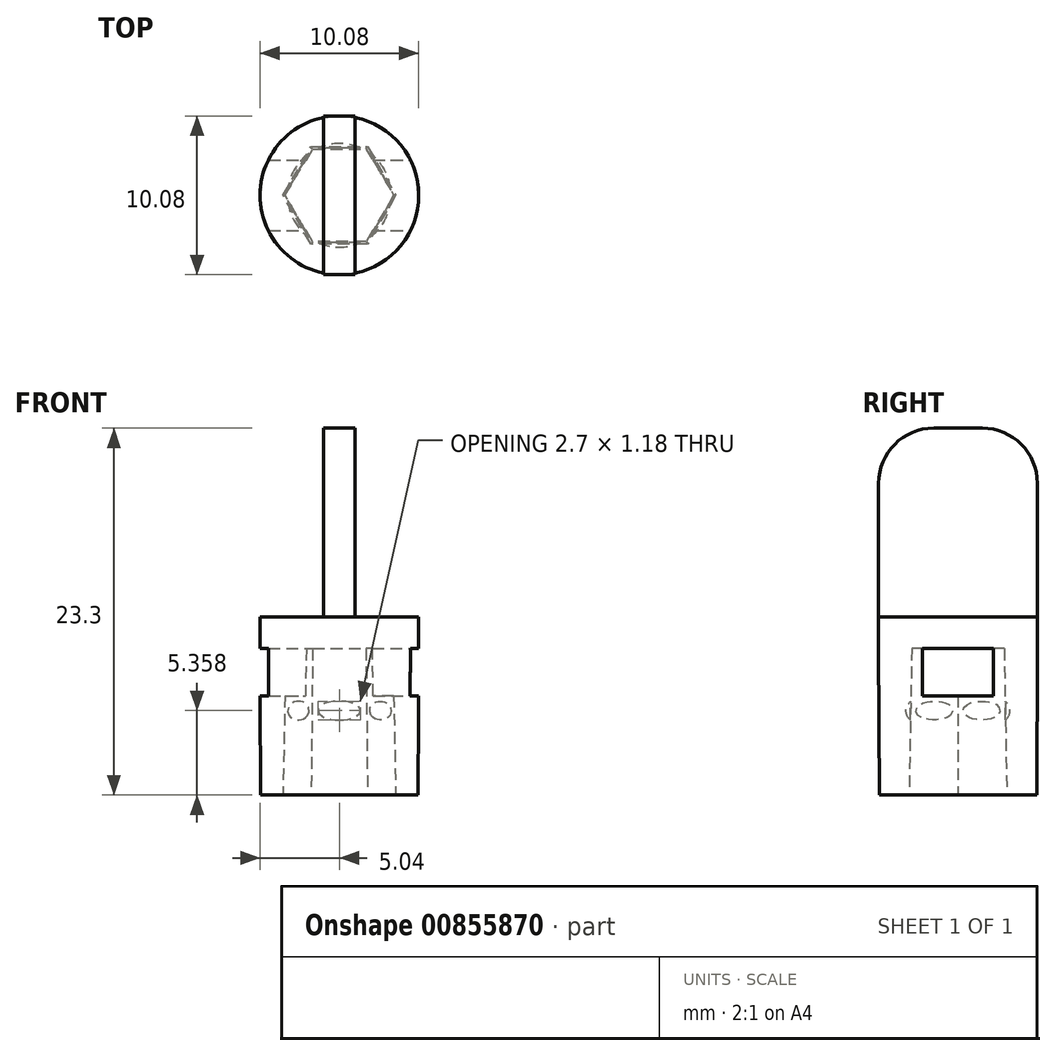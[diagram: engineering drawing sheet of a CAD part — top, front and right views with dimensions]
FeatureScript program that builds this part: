
annotation { "Feature Type Name" : "Feature", "Feature Type Description" : "" }
export const myFeature = defineFeature(function(context is Context, id is Id, definition is map)
    precondition{}
    {
        {
            var Q0;
            Q0=qCreatedBy(makeId("Top.planeOp"),FACE);
            var sketch = newSketch(context, id + "F0", { "sketchPlane" : qUnion([Q0])});
            skCircle(sketch, "E0.cCircle", {"center": v(0, 0) * mm, "radius": 3.1 * mm, "construction": true});
            skLineSegment(sketch, "E0.0", {"start": v(3.58, 0) * mm, "end": v(1.79, -3.1) * mm});
            skLineSegment(sketch, "E0.1", {"start": v(1.79, -3.1) * mm, "end": v(-1.79, -3.1) * mm});
            skLineSegment(sketch, "E0.2", {"start": v(-1.79, -3.1) * mm, "end": v(-3.58, 0) * mm});
            skLineSegment(sketch, "E0.3", {"start": v(-3.58, 0) * mm, "end": v(-1.79, 3.1) * mm});
            skLineSegment(sketch, "E0.4", {"start": v(-1.79, 3.1) * mm, "end": v(1.79, 3.1) * mm});
            skLineSegment(sketch, "E0.5", {"start": v(1.79, 3.1) * mm, "end": v(3.58, 0) * mm});
            skPoint(sketch, "E0.0.midPoint", {"position": v(2.68, -1.55) * mm});
            skCircle(sketch, "E1", {"center": v(0, 0) * mm, "radius": 5 * mm});
            skSolve(sketch);
        }
        {
            var Q0;
            Q0=makeQuery(id+"F0.imprint","IMPRINT",FACE,{"disambiguationData":[TD([[makeQuery(id+"F0.imprint","IMPRINT",EDGE,{"derivedFrom":sQuery(id+"F0.wireOp",EDGE,"E0.0")}),1.0]])]});
            var Q1;
            Q1=makeQuery(id+"F0.imprint","IMPRINT",FACE,{"disambiguationData":[TD([[makeQuery(id+"F0.imprint","IMPRINT",EDGE,{"derivedFrom":sQuery(id+"F0.wireOp",EDGE,"E0.0")}),-1.0]])]});
            extrude(context, id + "F1", {"entities" : qUnion([Q0, Q1]), "depth" : 9.3 * mm, "offsetDistance" : 25 * mm, "hasDraft" : true, "draftAngle" : .25 * degree});
        }
        {
            var Q0;
            Q0=qCreatedBy(makeId("Top.planeOp"),FACE);
            var sketch = newSketch(context, id + "F2", { "sketchPlane" : qUnion([Q0])});
            skCircle(sketch, "E2.cCircle", {"center": v(0, 0) * mm, "radius": 3.1 * mm, "construction": true});
            skLineSegment(sketch, "E2.0", {"start": v(3.58, 0) * mm, "end": v(1.79, -3.1) * mm});
            skLineSegment(sketch, "E2.1", {"start": v(1.79, -3.1) * mm, "end": v(-1.79, -3.1) * mm});
            skLineSegment(sketch, "E2.2", {"start": v(-1.79, -3.1) * mm, "end": v(-3.58, 0) * mm});
            skLineSegment(sketch, "E2.3", {"start": v(-3.58, 0) * mm, "end": v(-1.79, 3.1) * mm});
            skLineSegment(sketch, "E2.4", {"start": v(-1.79, 3.1) * mm, "end": v(1.79, 3.1) * mm});
            skLineSegment(sketch, "E2.5", {"start": v(1.79, 3.1) * mm, "end": v(3.58, 0) * mm});
            skPoint(sketch, "E2.0.midPoint", {"position": v(2.68, -1.55) * mm});
            skCircle(sketch, "E3", {"center": v(0, 0) * mm, "radius": 5 * mm});
            skSolve(sketch);
        }
        {
            var Q0;
            Q0=makeQuery(id+"F2.imprint","IMPRINT",FACE,{"disambiguationData":[TD([[makeQuery(id+"F2.imprint","IMPRINT",EDGE,{"derivedFrom":sQuery(id+"F2.wireOp",EDGE,"E2.0")}),-1.0]])]});
            extrude(context, id + "F3", {"entities" : qUnion([Q0]), "operationType" : NewBodyOperationType.REMOVE, "depth" : 9.3 * mm, "offsetDistance" : 25 * mm, "hasDraft" : true, "draftAngle" : 1 * degree, "draftPullDirection" : true});
        }
        {
            var Q0;
            Q0=qCreatedBy(makeId("Right.planeOp"),FACE);
            var sketch = newSketch(context, id + "F4", { "sketchPlane" : qUnion([Q0])});
            skLineSegment(sketch, "E4", {"start": v(0, 15.23) * mm, "end": v(0, -5.76) * mm, "construction": true});
            skCircle(sketch, "E5", {"center": v(-2.55, 5.35) * mm, "radius": 0.75 * mm});
            skLineSegment(sketch, "E6", {"start": v(12.61, 4.6) * mm, "end": v(-6.83, 4.6) * mm, "construction": true});
            skSolve(sketch);
        }
        {
            var Q0;
            Q0=makeQuery(id+"F4.imprint","IMPRINT",FACE,{"disambiguationData":[TD([[makeQuery(id+"F4.imprint","IMPRINT",EDGE,{"derivedFrom":sQuery(id+"F4.wireOp",EDGE,"E5")}),1.0]])]});
            var Q1;
            Q1=sQuery(id+"F4.wireOp",EDGE,"E4");
            revolve(context, id + "F5", {"operationType" : NewBodyOperationType.REMOVE, "surfaceOperationType" : NewSurfaceOperationType.NEW, "entities" : qUnion([Q0]), "axis" : qUnion([Q1]), "revolveType" : RevolveType.FULL, "oppositeDirection" : true});
        }
        {
            var Q0;
            Q0=qCreatedBy(makeId("Right.planeOp"),FACE);
            var sketch = newSketch(context, id + "F6", { "sketchPlane" : qUnion([Q0])});
            skLineSegment(sketch, "E7.bottom", {"start": v(2.25, 6.3) * mm, "end": v(-2.25, 6.3) * mm});
            skLineSegment(sketch, "E7.top", {"start": v(2.25, 9.3) * mm, "end": v(-2.25, 9.3) * mm});
            skLineSegment(sketch, "E7.left", {"start": v(2.25, 6.3) * mm, "end": v(2.25, 9.3) * mm});
            skLineSegment(sketch, "E7.right", {"start": v(-2.25, 6.3) * mm, "end": v(-2.25, 9.3) * mm});
            skPoint(sketch, "E7.middle", {"position": v(0, 7.8) * mm});
            skSolve(sketch);
        }
        {
            var Q0;
            Q0=makeQuery(id+"F6.imprint","IMPRINT",FACE,{"disambiguationData":[TD([[makeQuery(id+"F6.imprint","IMPRINT",EDGE,{"derivedFrom":sQuery(id+"F6.wireOp",EDGE,"E7.bottom")}),-1.0]])]});
            extrude(context, id + "F7", {"entities" : qUnion([Q0]), "operationType" : NewBodyOperationType.REMOVE, "oppositeDirection" : true, "depth" : 14.4 * mm, "offsetDistance" : 25 * mm, "symmetric" : true});
        }
        {
            var Q0;
            Q0=makeQuery(id+"F1.opExtrude","CAP_FACE",FACE,{"disambiguationData":[OSD([sQuery(id+"F0.wireOp",EDGE,"E0.0"),sQuery(id+"F0.wireOp",EDGE,"E0.1"),sQuery(id+"F0.wireOp",EDGE,"E0.2"),sQuery(id+"F0.wireOp",EDGE,"E0.3"),sQuery(id+"F0.wireOp",EDGE,"E0.4"),sQuery(id+"F0.wireOp",EDGE,"E0.5"),sQuery(id+"F0.wireOp",EDGE,"E1")])],"isStart":false});
            var sketch = newSketch(context, id + "F8", { "sketchPlane" : qUnion([Q0])});
            skCircle(sketch, "E8.0", {"center": v(0, 0) * mm, "radius": 5.04 * mm});
            skSolve(sketch);
        }
        {
            var Q0;
            Q0 = qSketchRegion(id + "F8", true);
            extrude(context, id + "F9", {"entities" : qUnion([Q0]), "operationType" : NewBodyOperationType.ADD, "depth" : 2 * mm, "offsetDistance" : 25 * mm});
        }
        {
            var Q0;
            Q0=qCreatedBy(makeId("Right.planeOp"),FACE);
            var sketch = newSketch(context, id + "F10", { "sketchPlane" : qUnion([Q0])});
            skLineSegment(sketch, "E9.0", {"start": v(-5.04, 11.3) * mm, "end": v(5.04, 11.3) * mm, "construction": true});
            skLineSegment(sketch, "E10.bottom", {"start": v(-5.04, 11.3) * mm, "end": v(5.04, 11.3) * mm});
            skLineSegment(sketch, "E10.top", {"start": v(-5.04, 23.3) * mm, "end": v(5.04, 23.3) * mm});
            skLineSegment(sketch, "E10.left", {"start": v(-5.04, 11.3) * mm, "end": v(-5.04, 23.3) * mm});
            skLineSegment(sketch, "E10.right", {"start": v(5.04, 11.3) * mm, "end": v(5.04, 23.3) * mm});
            skSolve(sketch);
        }
        {
            var Q0;
            Q0=makeQuery(id+"F10.imprint","IMPRINT",FACE,{"disambiguationData":[TD([[makeQuery(id+"F10.imprint","IMPRINT",EDGE,{"derivedFrom":sQuery(id+"F10.wireOp",EDGE,"E10.bottom")}),1.0]])]});
            extrude(context, id + "F11", {"entities" : qUnion([Q0]), "operationType" : NewBodyOperationType.ADD, "depth" : 2 * mm, "offsetDistance" : 25 * mm, "symmetric" : true});
        }
        {
            var Q0;
            Q0=makeQuery(id+"F11.opExtrude","SWEPT_EDGE",EDGE,{"disambiguationData":[OSD([sQuery(id+"F10.wireOp",EDGE,"E10.top"),sQuery(id+"F10.wireOp",EDGE,"E10.left")])]});
            var Q1;
            Q1=makeQuery(id+"F11.opExtrude","SWEPT_EDGE",EDGE,{"disambiguationData":[OSD([sQuery(id+"F10.wireOp",EDGE,"E10.top"),sQuery(id+"F10.wireOp",EDGE,"E10.right")])]});
            fillet(context, id + "F12", {"entities" : qUnion([Q0, Q1]), "radius" : 3.5 * mm, "tangentPropagation" : true, "allowEdgeOverflow" : false});
        }
    });
